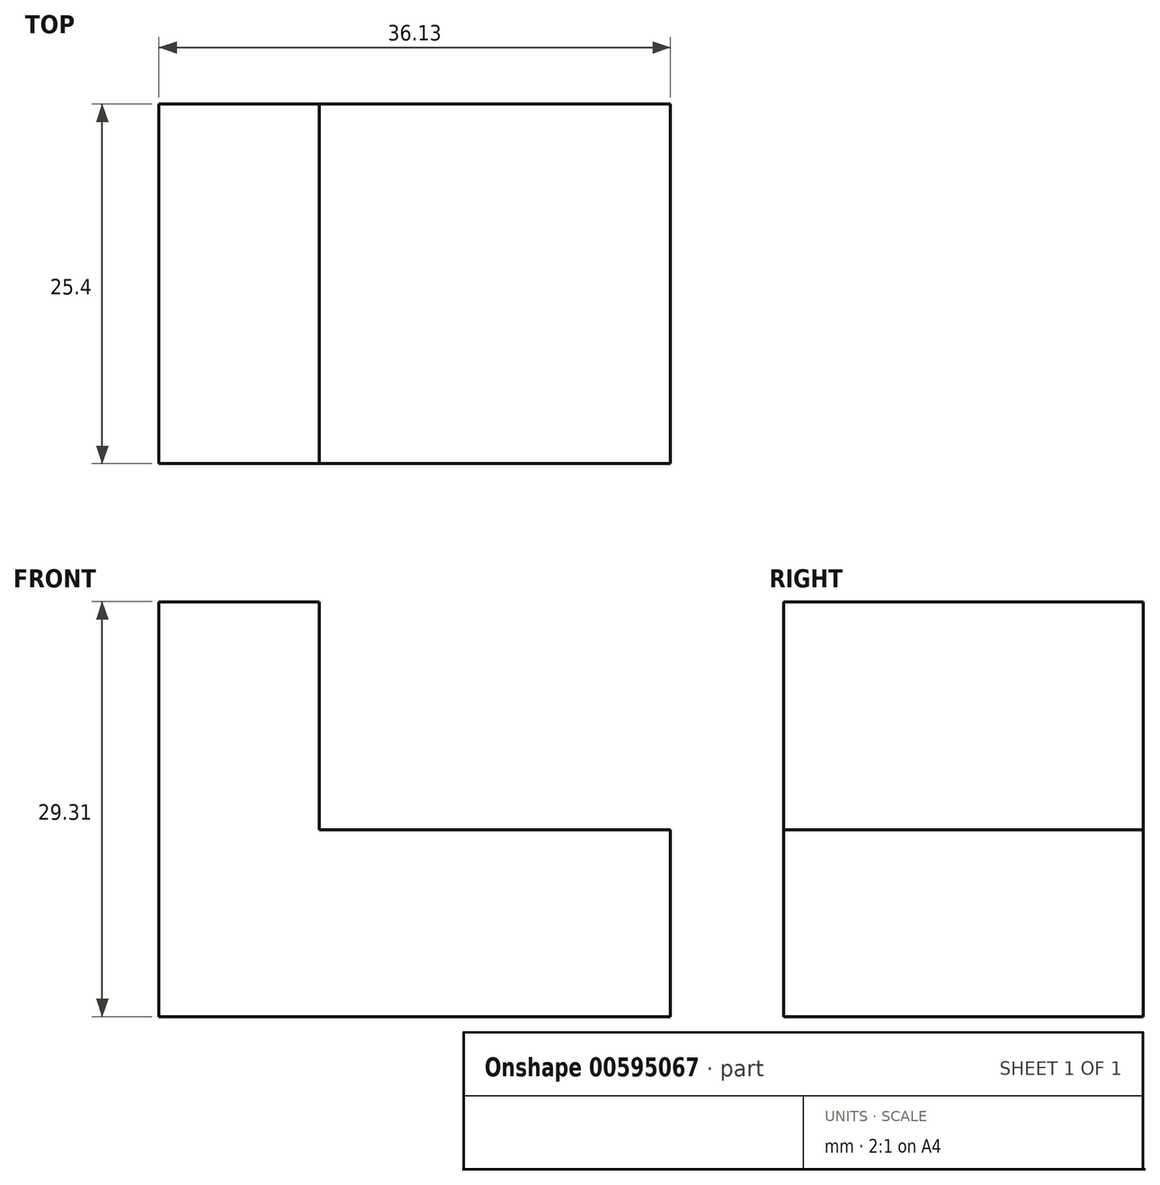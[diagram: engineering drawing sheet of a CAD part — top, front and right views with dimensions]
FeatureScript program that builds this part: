
annotation { "Feature Type Name" : "Feature", "Feature Type Description" : "" }
export const myFeature = defineFeature(function(context is Context, id is Id, definition is map)
    precondition{}
    {
        {
            var Q0;
            Q0=qCreatedBy(makeId("Front.planeOp"),FACE);
            var sketch = newSketch(context, id + "F0", { "sketchPlane" : qUnion([Q0])});
            skLineSegment(sketch, "E0", {"start": v(0, 0) * mm, "end": v(0, 29.3) * mm});
            skLineSegment(sketch, "E1", {"start": v(0, 29.3) * mm, "end": v(11.32, 29.3) * mm});
            skLineSegment(sketch, "E2", {"start": v(11.32, 29.3) * mm, "end": v(11.32, 13.18) * mm});
            skLineSegment(sketch, "E3", {"start": v(11.32, 13.18) * mm, "end": v(36.13, 13.18) * mm});
            skLineSegment(sketch, "E4", {"start": v(36.13, 13.18) * mm, "end": v(36.13, 0) * mm});
            skLineSegment(sketch, "E5", {"start": v(36.13, 0) * mm, "end": v(0, 0) * mm});
            skLineSegment(sketch, "E6", {"start": v(11.32, 13.18) * mm, "end": v(11.32, 7.9) * mm});
            skSolve(sketch);
        }
        {
            var Q0;
            Q0=makeQuery(id+"F0.imprint","IMPRINT",FACE,{"disambiguationData":[TD([[makeQuery(id+"F0.imprint","IMPRINT",EDGE,{"derivedFrom":sQuery(id+"F0.wireOp",EDGE,"E0")}),-1.0]])]});
            extrude(context, id + "F1", {"entities" : qUnion([Q0]), "depth" : 25.4 * mm, "offsetDistance" : 25.4 * mm});
        }
    });
